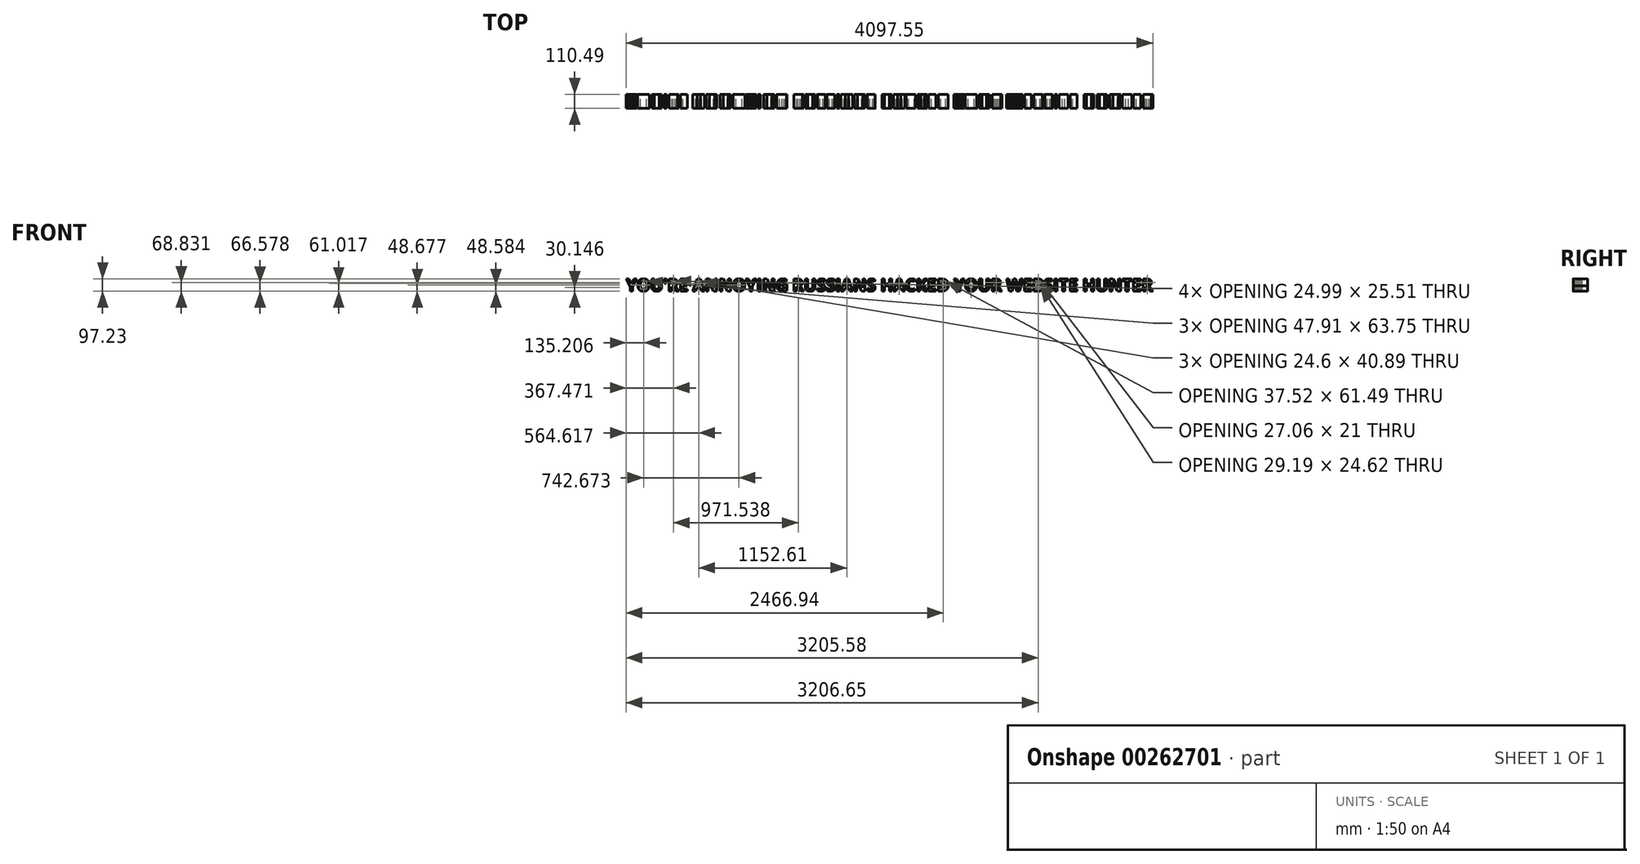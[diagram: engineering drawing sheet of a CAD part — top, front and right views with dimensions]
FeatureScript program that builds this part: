
annotation { "Feature Type Name" : "Feature", "Feature Type Description" : "" }
export const myFeature = defineFeature(function(context is Context, id is Id, definition is map)
    precondition{}
    {
        {
            var Q0;
            Q0=qCreatedBy(makeId("Front.planeOp"),FACE);
            var sketch = newSketch(context, id + "F0", { "sketchPlane" : qUnion([Q0])});
            skText(sketch, "E0", { "text": "YOU\'RE ANNOYING RUSSIANS HACKED YOUR WEBSITE HUNTER", "fontName": "OpenSans-Bold.ttf"});
            const initialGuessF0  = {"E0": [-0.11017, -0.06168, 1, 0, 0.09525]};
            skSetInitialGuess(sketch, initialGuessF0);
            skSolve(sketch);
        }
        {
            var Q0;
            Q0 = qSketchRegion(id + "F0", true);
            extrude(context, id + "F1", {"entities" : qUnion([Q0]), "depth" : 110.49 * mm});
        }
    });
